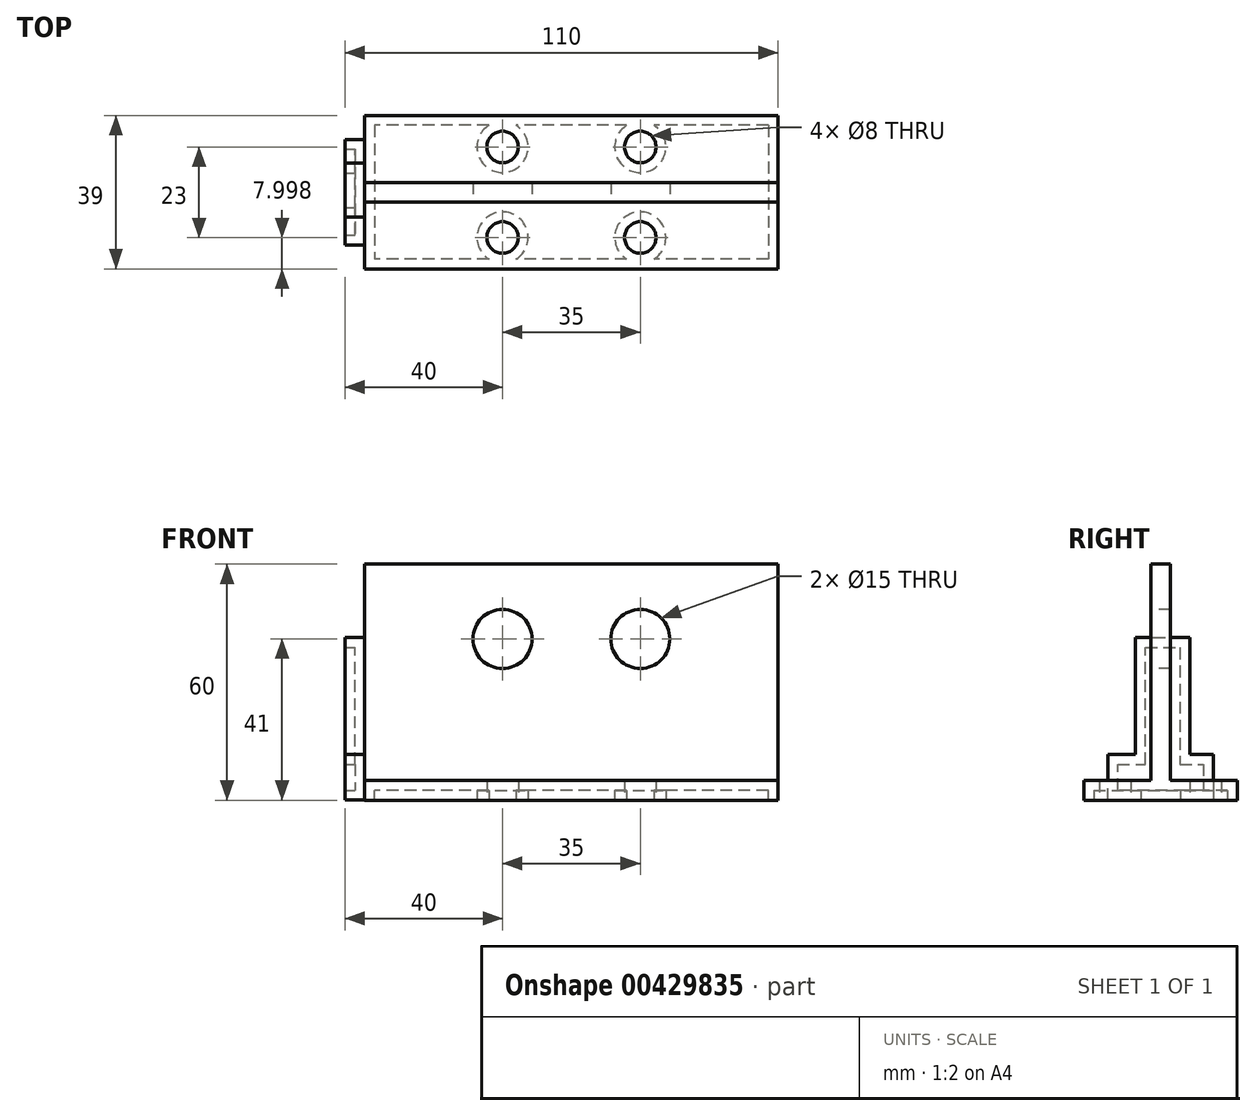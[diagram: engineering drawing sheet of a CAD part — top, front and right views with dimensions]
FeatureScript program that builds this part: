
annotation { "Feature Type Name" : "Feature", "Feature Type Description" : "" }
export const myFeature = defineFeature(function(context is Context, id is Id, definition is map)
    precondition{}
    {
        {
            var Q0;
            Q0=qCreatedBy(makeId("Right.planeOp"),FACE);
            var sketch = newSketch(context, id + "F0", { "sketchPlane" : qUnion([Q0])});
            skLineSegment(sketch, "E0", {"start": v(-13.31, 55) * mm, "end": v(-13.31, 0) * mm});
            skLineSegment(sketch, "E1", {"start": v(-13.31, -5) * mm, "end": v(-35.31, -5) * mm});
            skLineSegment(sketch, "E2", {"start": v(-35.31, -5) * mm, "end": v(-35.31, 0) * mm});
            skLineSegment(sketch, "E3", {"start": v(-35.31, 0) * mm, "end": v(-18.31, 0) * mm});
            skLineSegment(sketch, "E4", {"start": v(-18.31, 0) * mm, "end": v(-18.31, 55) * mm});
            skLineSegment(sketch, "E5", {"start": v(-13.31, 55) * mm, "end": v(-18.31, 55) * mm});
            skLineSegment(sketch, "E6.bottom", {"start": v(-13.31, -5) * mm, "end": v(3.69, -5) * mm});
            skLineSegment(sketch, "E6.top", {"start": v(-13.31, 0) * mm, "end": v(3.69, 0) * mm});
            skLineSegment(sketch, "E6.right", {"start": v(3.69, -5) * mm, "end": v(3.69, 0) * mm});
            skSolve(sketch);
        }
        {
            var Q0;
            Q0=makeQuery(id+"F0.imprint","IMPRINT",FACE,{"disambiguationData":[TD([[makeQuery(id+"F0.imprint","IMPRINT",EDGE,{"derivedFrom":sQuery(id+"F0.wireOp",EDGE,"E0")}),-1.0]])]});
            extrude(context, id + "F1", {"entities" : qUnion([Q0]), "endBound" : BoundingType.SYMMETRIC, "depth" : 105 * mm});
        }
        {
            var Q0;
            Q0=makeQuery(id+"F1.opExtrude","SWEPT_FACE",FACE,{"disambiguationData":[OSD([sQuery(id+"F0.wireOp",EDGE,"E1")])]});
            var sketch = newSketch(context, id + "F2", { "sketchPlane" : qUnion([Q0])});
            skPoint(sketch, "E7", {"position": v(-17.5, 4.31) * mm});
            skPoint(sketch, "E8", {"position": v(17.5, 4.31) * mm});
            skPoint(sketch, "E9", {"position": v(-17.5, 27.31) * mm});
            skPoint(sketch, "E10", {"position": v(17.5, 27.31) * mm});
            skSolve(sketch);
        }
        {
            var Q0;
            Q0=sQuery(id+"F2.wireOp",VERTEX,"E9");
            var Q1;
            Q1=sQuery(id+"F2.wireOp",VERTEX,"E10");
            var Q2;
            Q2=sQuery(id+"F2.wireOp",VERTEX,"E7");
            var Q3;
            Q3=sQuery(id+"F2.wireOp",VERTEX,"E8");
            var Q4;
            Q4=makeQuery(id+"F1.opExtrude","SWEPT_BODY",BODY,{"disambiguationData":[OSD([sQuery(id+"F0.wireOp",EDGE,"E0"),sQuery(id+"F0.wireOp",EDGE,"E1"),sQuery(id+"F0.wireOp",EDGE,"E2"),sQuery(id+"F0.wireOp",EDGE,"E3"),sQuery(id+"F0.wireOp",EDGE,"E4"),sQuery(id+"F0.wireOp",EDGE,"E5"),sQuery(id+"F0.wireOp",EDGE,"E6.bottom"),sQuery(id+"F0.wireOp",EDGE,"E6.top"),sQuery(id+"F0.wireOp",EDGE,"E6.right")])]});
            hole(context, id + "F3", {"style" : HoleStyle.SIMPLE, "endStyle" : HoleEndStyle.THROUGH, "holeDiameter" : 8 * mm, "isTappedThrough" : true, "tappedDepth" : 12 * mm, "tapClearance" : 3, "locations" : qUnion([Q0, Q1, Q2, Q3]), "scope" : qUnion([Q4])});
        }
        {
            var Q0;
            Q0=makeQuery(id+"F1.opExtrude","CAP_FACE",FACE,{"disambiguationData":[OSD([sQuery(id+"F0.wireOp",EDGE,"E0"),sQuery(id+"F0.wireOp",EDGE,"E1"),sQuery(id+"F0.wireOp",EDGE,"E2"),sQuery(id+"F0.wireOp",EDGE,"E3"),sQuery(id+"F0.wireOp",EDGE,"E4"),sQuery(id+"F0.wireOp",EDGE,"E5"),sQuery(id+"F0.wireOp",EDGE,"E6.bottom"),sQuery(id+"F0.wireOp",EDGE,"E6.top"),sQuery(id+"F0.wireOp",EDGE,"E6.right")])],"isStart":true});
            cPlane(context, id + "F4", {"entities" : qUnion([Q0]), "cplaneType" : CPlaneType.OFFSET, "offset" : 0 * mm, "oppositeDirection" : true, "width" : 150 * mm, "height" : 150 * mm});
        }
        {
            var Q0;
            Q0=makeQuery(id+"F1.opExtrude","SWEPT_FACE",FACE,{"disambiguationData":[OSD([sQuery(id+"F0.wireOp",EDGE,"E4")])]});
            var sketch = newSketch(context, id + "F5", { "sketchPlane" : qUnion([Q0])});
            skPoint(sketch, "E11", {"position": v(-17.5, 36) * mm});
            skPoint(sketch, "E12", {"position": v(17.5, 36) * mm});
            skSolve(sketch);
        }
        {
            var Q0;
            Q0=sQuery(id+"F5.wireOp",VERTEX,"E12");
            var Q1;
            Q1=sQuery(id+"F5.wireOp",VERTEX,"E11");
            var Q2;
            Q2=makeQuery(id+"F1.opExtrude","SWEPT_BODY",BODY,{"disambiguationData":[OSD([sQuery(id+"F0.wireOp",EDGE,"E0"),sQuery(id+"F0.wireOp",EDGE,"E1"),sQuery(id+"F0.wireOp",EDGE,"E2"),sQuery(id+"F0.wireOp",EDGE,"E3"),sQuery(id+"F0.wireOp",EDGE,"E4"),sQuery(id+"F0.wireOp",EDGE,"E5"),sQuery(id+"F0.wireOp",EDGE,"E6.bottom"),sQuery(id+"F0.wireOp",EDGE,"E6.top"),sQuery(id+"F0.wireOp",EDGE,"E6.right")])]});
            hole(context, id + "F6", {"style" : HoleStyle.SIMPLE, "endStyle" : HoleEndStyle.THROUGH, "holeDiameter" : 15 * mm, "isTappedThrough" : true, "tappedDepth" : 12 * mm, "tapClearance" : 3, "locations" : qUnion([Q0, Q1]), "scope" : qUnion([Q2])});
        }
        {
            var Q0;
            Q0=qCreatedBy(id+"F4.planeOp",FACE);
            var sketch = newSketch(context, id + "F7", { "sketchPlane" : qUnion([Q0])});
            skLineSegment(sketch, "E13", {"start": v(2.38, -4.92) * mm, "end": v(29.2, -4.92) * mm});
            skLineSegment(sketch, "E14", {"start": v(29.2, -4.92) * mm, "end": v(29.2, 6.65) * mm});
            skLineSegment(sketch, "E15", {"start": v(29.2, 6.65) * mm, "end": v(22.18, 6.65) * mm});
            skLineSegment(sketch, "E16", {"start": v(22.18, 6.65) * mm, "end": v(22.18, 36.32) * mm});
            skLineSegment(sketch, "E17", {"start": v(22.18, 36.32) * mm, "end": v(8.43, 36.32) * mm});
            skLineSegment(sketch, "E18", {"start": v(8.43, 36.32) * mm, "end": v(8.43, 6.65) * mm});
            skLineSegment(sketch, "E19", {"start": v(8.43, 6.65) * mm, "end": v(2.38, 6.65) * mm});
            skLineSegment(sketch, "E20", {"start": v(2.38, 6.65) * mm, "end": v(2.38, -4.92) * mm});
            skSolve(sketch);
        }
        {
            var Q0;
            Q0=makeQuery(id+"F7.imprint","IMPRINT",FACE,{"disambiguationData":[TD([[makeQuery(id+"F7.imprint","IMPRINT",EDGE,{"derivedFrom":sQuery(id+"F7.wireOp",EDGE,"E13")}),1.0]])]});
            extrude(context, id + "F8", {"entities" : qUnion([Q0]), "depth" : 5 * mm});
        }
        {
            var Q0;
            Q0=makeQuery(id+"F8.opExtrude","CAP_FACE",FACE,{"disambiguationData":[OSD([sQuery(id+"F7.wireOp",EDGE,"E13"),sQuery(id+"F7.wireOp",EDGE,"E14"),sQuery(id+"F7.wireOp",EDGE,"E15"),sQuery(id+"F7.wireOp",EDGE,"E16"),sQuery(id+"F7.wireOp",EDGE,"E17"),sQuery(id+"F7.wireOp",EDGE,"E18"),sQuery(id+"F7.wireOp",EDGE,"E19"),sQuery(id+"F7.wireOp",EDGE,"E20")])],"isStart":false});
            shell(context, id + "F9", {"entities" : qUnion([Q0]), "thickness" : 2.5 * mm});
        }
        {
            var Q0;
            Q0=makeQuery(id+"F1.opExtrude","SWEPT_FACE",FACE,{"disambiguationData":[OSD([sQuery(id+"F0.wireOp",EDGE,"E1"),sQuery(id+"F0.wireOp",EDGE,"E6.bottom")])]});
            shell(context, id + "F10", {"entities" : qUnion([Q0]), "thickness" : 2.5 * mm});
        }
    });
